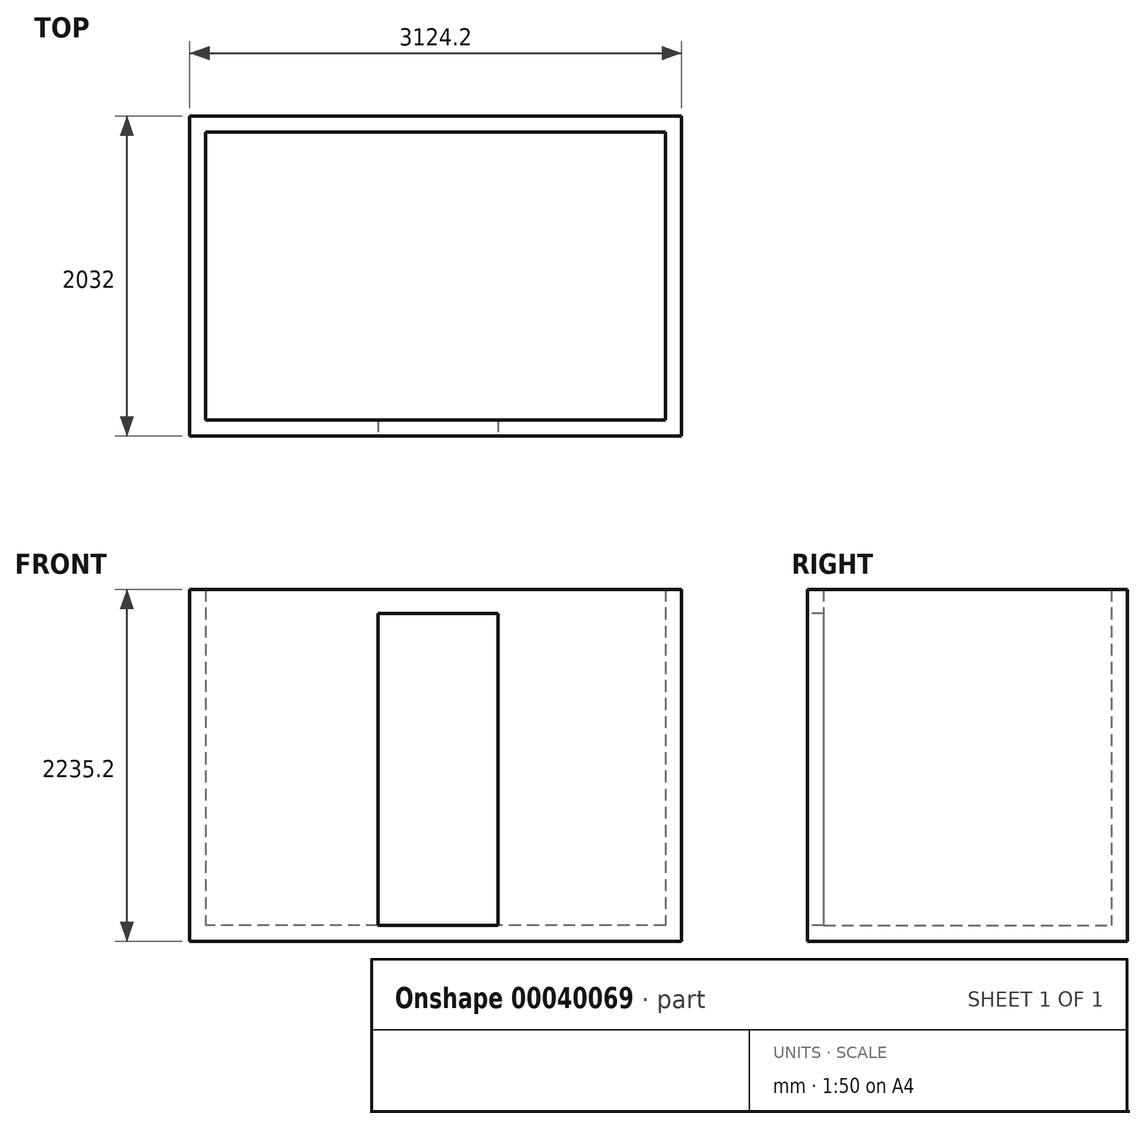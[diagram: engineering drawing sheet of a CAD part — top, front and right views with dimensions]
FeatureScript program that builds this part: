
annotation { "Feature Type Name" : "Feature", "Feature Type Description" : "" }
export const myFeature = defineFeature(function(context is Context, id is Id, definition is map)
    precondition{}
    {
        {
            var Q0;
            Q0=qCreatedBy(makeId("Top.planeOp"),FACE);
            var sketch = newSketch(context, id + "F0", { "sketchPlane" : qUnion([Q0])});
            skLineSegment(sketch, "E0.rect.bottom", {"start": v(1460.5, -914.4) * mm, "end": v(-1460.5, -914.4) * mm});
            skLineSegment(sketch, "E0.rect.top", {"start": v(1460.5, 914.4) * mm, "end": v(-1460.5, 914.4) * mm});
            skLineSegment(sketch, "E0.rect.left", {"start": v(1460.5, -914.4) * mm, "end": v(1460.5, 914.4) * mm});
            skLineSegment(sketch, "E0.rect.right", {"start": v(-1460.5, -914.4) * mm, "end": v(-1460.5, 914.4) * mm});
            skPoint(sketch, "E0.rect.middle", {"position": v(0, 0) * mm});
            skSolve(sketch);
        }
        {
            var Q0;
            Q0=qSketchRegion(id+"F0",true);
            extrude(context, id + "F1", {"entities" : qUnion([Q0]), "depth" : 2133.6 * mm});
        }
        {
            var Q0;
            Q0=makeQuery(id+"F1.opExtrude","CAP_FACE",FACE,{"disambiguationData":[OSD([sQuery(id+"F0.wireOp",EDGE,"E0.rect.bottom"),sQuery(id+"F0.wireOp",EDGE,"E0.rect.top"),sQuery(id+"F0.wireOp",EDGE,"E0.rect.left"),sQuery(id+"F0.wireOp",EDGE,"E0.rect.right")])],"isStart":false});
            var Q1;
            Q1=makeQuery(id+"F1.opExtrude","SWEPT_BODY",BODY,{"disambiguationData":[OSD([sQuery(id+"F0.wireOp",EDGE,"E0.rect.bottom"),sQuery(id+"F0.wireOp",EDGE,"E0.rect.top"),sQuery(id+"F0.wireOp",EDGE,"E0.rect.left"),sQuery(id+"F0.wireOp",EDGE,"E0.rect.right")])]});
            shell(context, id + "F2", {"entities" : qUnion([Q0]), "parts" : qUnion([Q1]), "thickness" : 101.6 * mm, "oppositeDirection" : true});
        }
        {
            var Q0;
            Q0=makeQuery(id+"F1.opExtrude","SWEPT_FACE",FACE,{"disambiguationData":[OSD([sQuery(id+"F0.wireOp",EDGE,"E0.rect.bottom")])]});
            var sketch = newSketch(context, id + "F3", { "sketchPlane" : qUnion([Q0])});
            skLineSegment(sketch, "E1.bottom", {"start": v(-367.73, 0) * mm, "end": v(394.27, 0) * mm});
            skLineSegment(sketch, "E1.top", {"start": v(-367.73, 1981.2) * mm, "end": v(394.27, 1981.2) * mm});
            skLineSegment(sketch, "E1.left", {"start": v(-367.73, 0) * mm, "end": v(-367.73, 1981.2) * mm});
            skLineSegment(sketch, "E1.right", {"start": v(394.27, 0) * mm, "end": v(394.27, 1981.2) * mm});
            skSolve(sketch);
        }
        {
            var Q0;
            Q0=qSketchRegion(id+"F3",true);
            extrude(context, id + "F4", {"entities" : qUnion([Q0]), "operationType" : NewBodyOperationType.REMOVE, "endBound" : BoundingType.UP_TO_NEXT, "oppositeDirection" : true, "depth" : 25.4 * mm});
        }
    });
